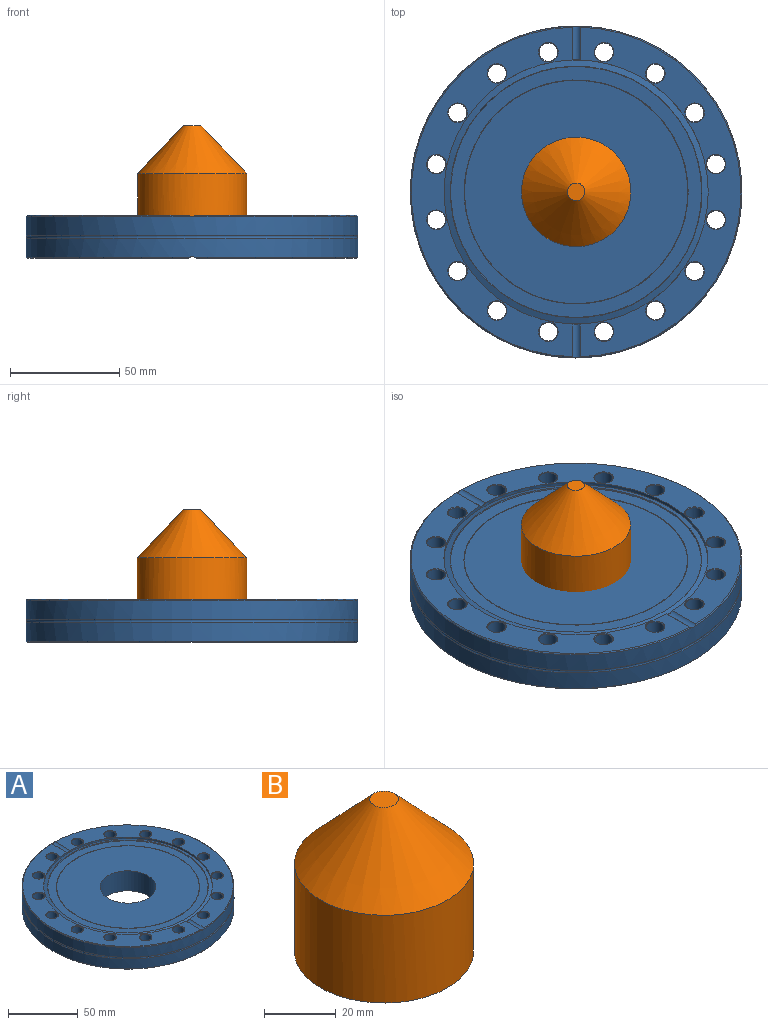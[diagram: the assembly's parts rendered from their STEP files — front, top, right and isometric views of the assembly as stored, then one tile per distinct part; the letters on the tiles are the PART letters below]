
ASSEMBLY  parts=2 mates=1
PART A: 78 faces, bbox 164.2x164.2x19.8 mm
  f0: cylinder r=75.82mm len=151.64mm, axis (0,0,1), area 4156.9mm2, adj f1,f67,f68,f69,f71
  f1: cylinder r=2.38mm len=15.51mm, axis (0,-1,0), area 61.7mm2, adj f0,f2,f3,f53,f69,f71
  f2: plane 150.58x73.54mm, normal (0,0,-1), area 2637.4mm2, adj f1,f3,f6,f9,f12,f15,f42,f45
  f3: cylinder r=60.32mm len=120.65mm, axis (0,0,1), area 642.8mm2, adj f1,f2,f53,f58,f67
  f4: cylinder r=60.32mm len=120.65mm, axis (0,0,-1), area 642.8mm2, adj f50,f51,f56,f63,f66
  f5: cone r=4.47mm half-angle=45deg, axis (0,0,1), area 9.8mm2, adj f7,f50
  f6: cone r=4.47mm half-angle=45deg, axis (0,0,-1), area 9.8mm2, adj f2,f7
  f7: cylinder r=4.22mm len=19.3mm, axis (0,0,1), area 511.4mm2, adj f5,f6
  f8: cone r=4.47mm half-angle=45deg, axis (0,0,1), area 9.8mm2, adj f10,f50
  f9: cone r=4.47mm half-angle=45deg, axis (0,0,-1), area 9.8mm2, adj f2,f10
  f10: cylinder r=4.22mm len=19.3mm, axis (0,0,1), area 511.4mm2, adj f8,f9
  f11: cone r=4.47mm half-angle=45deg, axis (0,0,1), area 9.8mm2, adj f13,f50
  f12: cone r=4.47mm half-angle=45deg, axis (0,0,-1), area 9.8mm2, adj f2,f13
  f13: cylinder r=4.22mm len=19.3mm, axis (0,0,1), area 511.4mm2, adj f11,f12
  f14: cone r=4.47mm half-angle=45deg, axis (0,0,1), area 9.8mm2, adj f16,f50
  f15: cone r=4.47mm half-angle=45deg, axis (0,0,-1), area 9.8mm2, adj f2,f16
  f16: cylinder r=4.22mm len=19.3mm, axis (0,0,1), area 511.4mm2, adj f14,f15
  f17: cone r=4.47mm half-angle=45deg, axis (0,0,1), area 9.8mm2, adj f19,f51
  f18: cone r=4.47mm half-angle=45deg, axis (0,0,-1), area 9.8mm2, adj f19,f53
  f19: cylinder r=4.22mm len=19.3mm, axis (0,0,1), area 511.4mm2, adj f17,f18
  f20: cone r=4.47mm half-angle=45deg, axis (0,0,1), area 9.8mm2, adj f22,f51
  f21: cone r=4.47mm half-angle=45deg, axis (0,0,-1), area 9.8mm2, adj f22,f53
  f22: cylinder r=4.22mm len=19.3mm, axis (0,0,1), area 511.4mm2, adj f20,f21
  f23: cone r=4.47mm half-angle=45deg, axis (0,0,1), area 9.8mm2, adj f25,f51
  f24: cone r=4.47mm half-angle=45deg, axis (0,0,-1), area 9.8mm2, adj f25,f53
  f25: cylinder r=4.22mm len=19.3mm, axis (0,0,1), area 511.4mm2, adj f23,f24
  f26: cone r=4.47mm half-angle=45deg, axis (0,0,1), area 9.8mm2, adj f28,f51
  f27: cone r=4.47mm half-angle=45deg, axis (0,0,-1), area 9.8mm2, adj f28,f53
  f28: cylinder r=4.22mm len=19.3mm, axis (0,0,1), area 511.4mm2, adj f26,f27
  f29: cone r=4.47mm half-angle=45deg, axis (0,0,1), area 9.8mm2, adj f31,f51
  f30: cone r=4.47mm half-angle=45deg, axis (0,0,-1), area 9.8mm2, adj f31,f53
  f31: cylinder r=4.22mm len=19.3mm, axis (0,0,1), area 511.4mm2, adj f29,f30
  f32: cone r=4.47mm half-angle=45deg, axis (0,0,1), area 9.8mm2, adj f34,f51
  f33: cone r=4.47mm half-angle=45deg, axis (0,0,-1), area 9.8mm2, adj f34,f53
  f34: cylinder r=4.22mm len=19.3mm, axis (0,0,1), area 511.4mm2, adj f32,f33
  f35: cone r=4.47mm half-angle=45deg, axis (0,0,1), area 9.8mm2, adj f37,f51
  f36: cone r=4.47mm half-angle=45deg, axis (0,0,-1), area 9.8mm2, adj f37,f53
  f37: cylinder r=4.22mm len=19.3mm, axis (0,0,1), area 511.4mm2, adj f35,f36
  f38: cone r=4.47mm half-angle=45deg, axis (0,0,1), area 9.8mm2, adj f40,f51
  f39: cone r=4.47mm half-angle=45deg, axis (0,0,-1), area 9.8mm2, adj f40,f53
  f40: cylinder r=4.22mm len=19.3mm, axis (0,0,1), area 511.4mm2, adj f38,f39
  f41: cone r=4.47mm half-angle=45deg, axis (0,0,1), area 9.8mm2, adj f43,f50
  f42: cone r=4.47mm half-angle=45deg, axis (0,0,-1), area 9.8mm2, adj f2,f43
  f43: cylinder r=4.22mm len=19.3mm, axis (0,0,1), area 511.4mm2, adj f41,f42
  f44: cone r=4.47mm half-angle=45deg, axis (0,0,1), area 9.8mm2, adj f46,f50
  f45: cone r=4.47mm half-angle=45deg, axis (0,0,-1), area 9.8mm2, adj f2,f46
  f46: cylinder r=4.22mm len=19.3mm, axis (0,0,1), area 511.4mm2, adj f44,f45
  f47: cone r=4.47mm half-angle=45deg, axis (0,0,1), area 9.8mm2, adj f49,f50
  f48: cone r=4.47mm half-angle=45deg, axis (0,0,-1), area 9.8mm2, adj f2,f49
  f49: cylinder r=4.22mm len=19.3mm, axis (0,0,1), area 511.4mm2, adj f47,f48
  f50: plane 150.58x73.54mm, normal (0,0,1), area 2637.5mm2, adj f4,f5,f8,f11,f14,f41,f44,f47
  f51: plane 150.58x73.54mm, normal (0,0,1), area 2637.5mm2, adj f4,f17,f20,f23,f26,f29,f32,f35
  f52: cylinder r=75.82mm len=151.64mm, axis (0,0,1), area 4156.9mm2, adj f63,f64,f65,f66,f68
  f53: plane 150.58x73.54mm, normal (0,0,-1), area 2637.4mm2, adj f1,f3,f18,f21,f24,f27,f30,f33
  f54: plane 114.59x114.59mm, normal (0,0,1), area 2083.7mm2, adj f55,f72
  f55: cone r=57.3mm half-angle=20deg, axis (0,0,1), area 194.9mm2, adj f54,f56
  f56: cone r=57.48mm half-angle=70deg, axis (0,0,-1), area 1120.4mm2, adj f4,f55
  f57: plane 114.59x114.59mm, normal (0,0,-1), area 2083.7mm2, adj f59,f70
  f58: cone r=60.32mm half-angle=70deg, axis (0,0,1), area 1120.4mm2, adj f3,f59
  f59: cone r=57.48mm half-angle=20deg, axis (0,0,-1), area 194.9mm2, adj f57,f58
  f60: cylinder r=4.22mm len=19.3mm, axis (0,0,1), area 511.4mm2, adj f61,f62
  f61: cone r=4.47mm half-angle=45deg, axis (0,0,1), area 9.8mm2, adj f50,f60
  f62: cone r=4.47mm half-angle=45deg, axis (0,0,-1), area 9.8mm2, adj f2,f60
  f63: cylinder r=2.38mm len=15.51mm, axis (0,1,0), area 61.4mm2, adj f4,f50,f51,f52,f64,f65
  f64: cone r=75.82mm half-angle=45deg, axis (0,0,-1), area 168.5mm2, adj f50,f52,f63,f66
  f65: cone r=75.82mm half-angle=45deg, axis (0,0,-1), area 168.5mm2, adj f51,f52,f63,f66
  f66: cylinder r=2.38mm len=15.51mm, axis (0,-1,0), area 61.7mm2, adj f4,f50,f51,f52,f64,f65
  f67: cylinder r=2.38mm len=15.51mm, axis (0,1,0), area 61.7mm2, adj f0,f2,f3,f53,f69,f71
  f68: torus R=76.58mm, axis (0,0,-1), area 698.1mm2, adj f0,f52
  f69: cone r=75.31mm half-angle=45deg, axis (0,0,1), area 168.5mm2, adj f0,f1,f53,f67
  f70: torus R=51.18mm, axis (0,0,1), area 56.8mm2, adj f57,f75
  f71: cone r=75.31mm half-angle=45deg, axis (0,0,1), area 168.5mm2, adj f0,f1,f2,f67
  f72: torus R=51.18mm, axis (0,0,1), area 56.8mm2, adj f54,f74
  f73: plane 102.04x102.04mm, normal (0,0,1), area 6920.5mm2, adj f74,f77
  f74: cylinder r=51.02mm len=102.04mm, axis (0,0,-1), area 26.9mm2, adj f72,f73
  f75: cylinder r=51.02mm len=102.04mm, axis (0,0,-1), area 18.9mm2, adj f70,f76
  f76: plane 102.04x102.04mm, normal (0,0,-1), area 6920.5mm2, adj f75,f77
  f77: cylinder r=20mm len=40mm, axis (0,0,-1), area 2199.1mm2, adj f73,f76
PART B: 7 faces, bbox 50x50x52 mm
  f0: cylinder r=23mm len=46mm, axis (0,0,-1), area 4335.4mm2, adj f2,f5
  f1: cylinder r=25mm len=50mm, axis (0,0,-1), area 4712.4mm2, adj f2,f4
  f2: plane 50x50mm, normal (0,0,-1), area 301.6mm2, adj f0,f1
  f3: plane 8x8mm, normal (0,0,1), area 50.3mm2, adj f4
  f4: cone r=4mm half-angle=43.7deg, axis (0,0,-1), area 2770.9mm2, adj f1,f3
  f5: cone r=23mm half-angle=43.5deg, axis (0,0,-1), area 2254.1mm2, adj f0,f6
  f6: plane 11.8x11.8mm, normal (0,0,-1), area 109.4mm2, adj f5
PLACE A t=(-0.58,-0.16,-4.2)mm
PLACE B t=(-0.58,-0.16,-5.44)mm
MATE parallel B.f1 <-> A.f77  axis (0,0,-1) through (-0.58,-0.16,-5.44)mm
